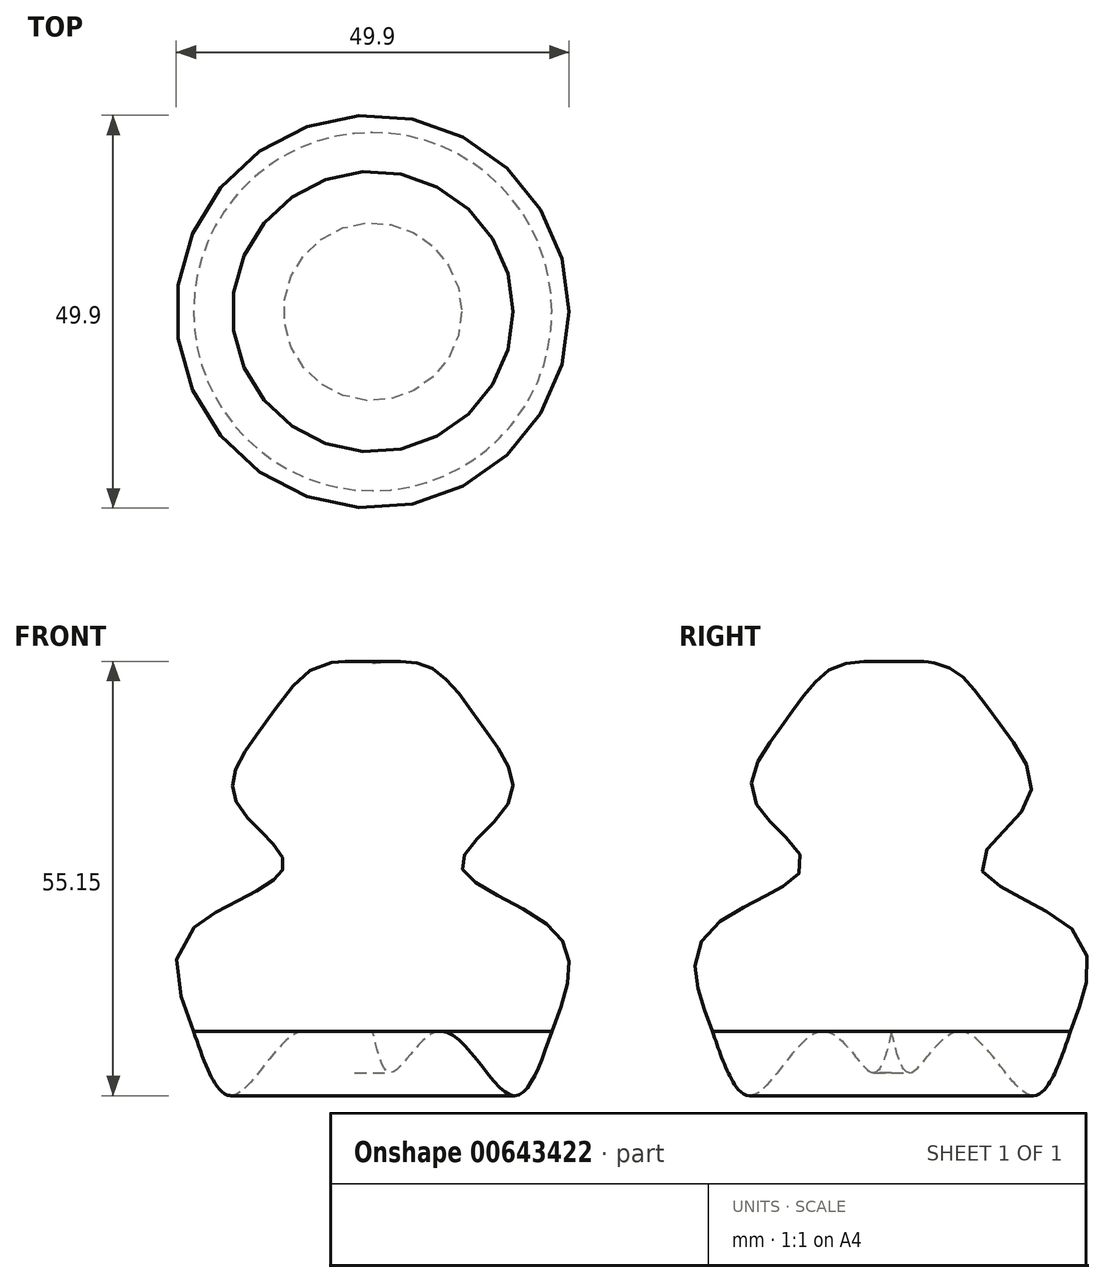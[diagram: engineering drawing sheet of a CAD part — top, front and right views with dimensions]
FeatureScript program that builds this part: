
annotation { "Feature Type Name" : "Feature", "Feature Type Description" : "" }
export const myFeature = defineFeature(function(context is Context, id is Id, definition is map)
    precondition{}
    {
        {
            var Q0;
            Q0=qCreatedBy(makeId("Front.planeOp"),FACE);
            var sketch = newSketch(context, id + "F0", { "sketchPlane" : qUnion([Q0])});
            skLineSegment(sketch, "E0", {"start": v(0, 0) * mm, "end": v(0, 46.7) * mm});
            skFitSpline(sketch, "E1", {"points": [v(22.76, 0) * mm, v(23.47, 12.4) * mm, v(11.32, 20.97) * mm, v(17.51, 29.55) * mm, v(13.7, 39.08) * mm, v(7.27, 46.23) * mm, v(0, 46.7) * mm], "startDerivative": vector(29.55, 76.08) * mm, "endDerivative": vector(-56.33, -6.07) * mm});
            skFitSpline(sketch, "E2", {"points": [v(22.76, 0) * mm, v(17.51, -8.1) * mm, v(8.7, 0) * mm, v(2.5, -5.24) * mm, v(0, 0) * mm], "startDerivative": vector(-17.3, -50.5) * mm, "endDerivative": vector(-9.4, 41.24) * mm});
            skSolve(sketch);
        }
        {
            var Q0;
            Q0=makeQuery(id+"F0.imprint","IMPRINT",FACE,{"disambiguationData":[TD([[makeQuery(id+"F0.imprint","IMPRINT",EDGE,{"derivedFrom":sQuery(id+"F0.wireOp",EDGE,"E0")}),-1.0]])]});
            var Q1;
            Q1=sQuery(id+"F0.wireOp",EDGE,"E1");
            var Q2;
            Q2=sQuery(id+"F0.wireOp",EDGE,"E2");
            var Q3;
            Q3=sQuery(id+"F0.wireOp",EDGE,"E0");
            revolve(context, id + "F1", {"bodyType" : ToolBodyType.SURFACE, "entities" : qUnion([Q0]), "surfaceEntities" : qUnion([Q1, Q2]), "axis" : qUnion([Q3]), "revolveType" : RevolveType.FULL});
        }
    });
